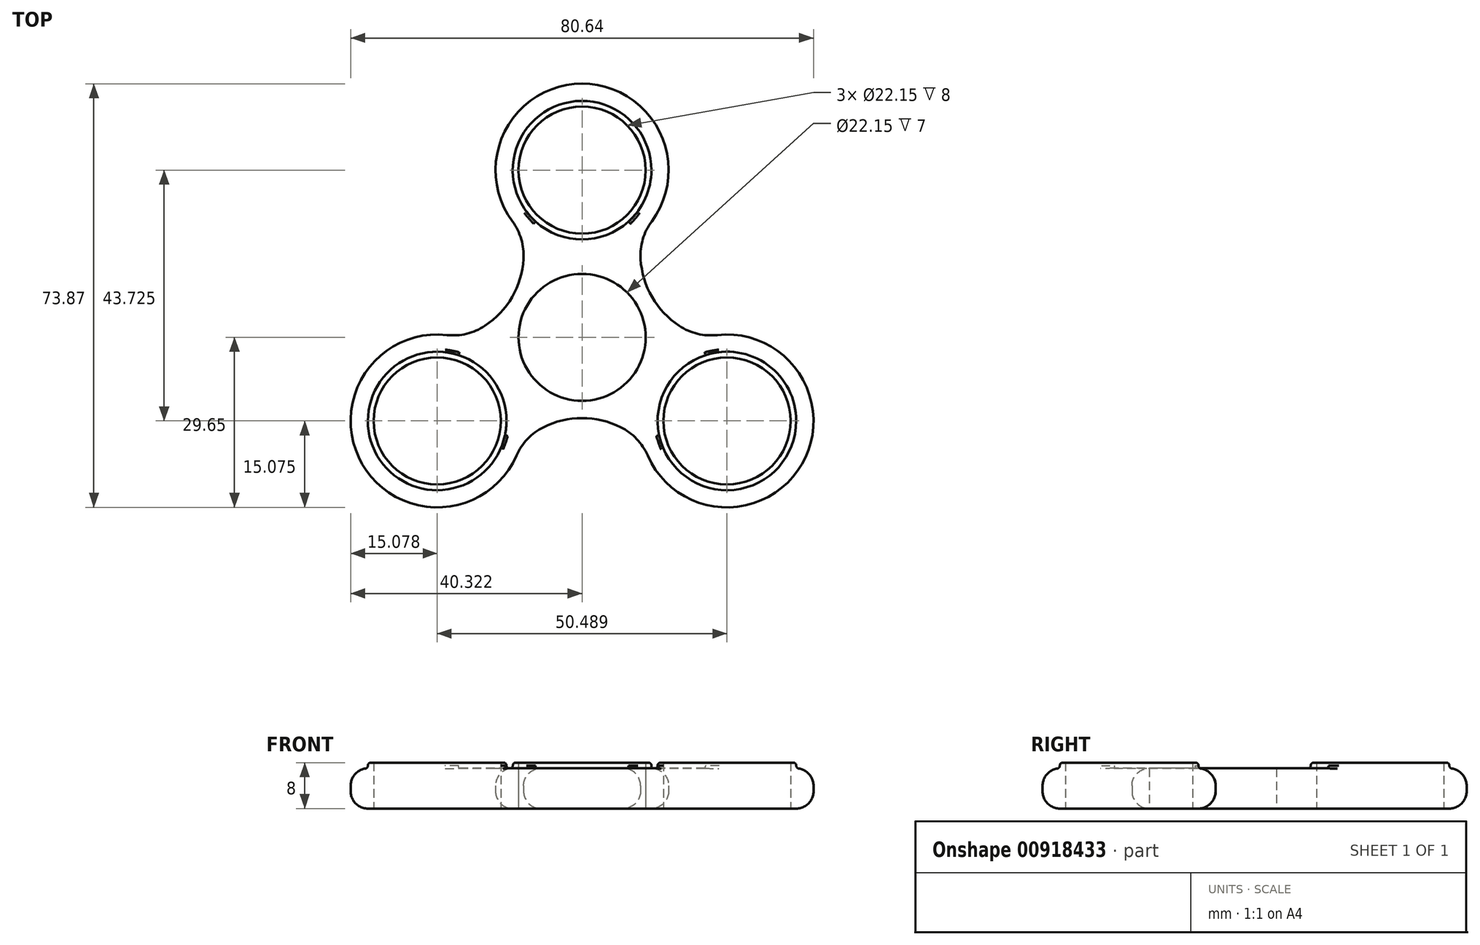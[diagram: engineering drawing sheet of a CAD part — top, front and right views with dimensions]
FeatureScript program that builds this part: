
annotation { "Feature Type Name" : "Feature", "Feature Type Description" : "" }
export const myFeature = defineFeature(function(context is Context, id is Id, definition is map)
    precondition{}
    {
        {
            var Q0;
            Q0=qCreatedBy(makeId("Top.planeOp"),FACE);
            var sketch = newSketch(context, id + "F0", { "sketchPlane" : qUnion([Q0])});
            skCircle(sketch, "E0", {"center": v(-80.48, 0) * mm, "radius": 11.07 * mm});
            skCircle(sketch, "E1", {"center": v(-80.48, 29.15) * mm, "radius": 11.07 * mm});
            skArc(sketch, "E2.0", {"start": v(-69.78, 18.53) * mm, "mid": v(-80.48, 44.23) * mm, "end": v(-91.17, 18.53) * mm});
            skArc(sketch, "E3.0", {"start": v(-69.78, -18.53) * mm, "mid": v(-80.48, -14.08) * mm, "end": v(-91.17, -18.53) * mm});
            skArc(sketch, "E4.0", {"start": v(-69.78, 18.53) * mm, "mid": v(-68.29, 7.04) * mm, "end": v(-59.08, 0) * mm});
            skCircle(sketch, "E5", {"center": v(-105.72, -14.58) * mm, "radius": 11.07 * mm});
            skArc(sketch, "E6.0", {"start": v(-101.87, 0) * mm, "mid": v(-118.78, -22.11) * mm, "end": v(-91.17, -18.53) * mm});
            skLineSegment(sketch, "E7.0", {"start": v(-105.72, -14.58) * mm, "end": v(-55.23, 14.58) * mm, "construction": true});
            skArc(sketch, "E8.0", {"start": v(-101.87, 0) * mm, "mid": v(-92.67, 7.04) * mm, "end": v(-91.17, 18.53) * mm});
            skCircle(sketch, "E9", {"center": v(-55.23, -14.58) * mm, "radius": 11.07 * mm});
            skArc(sketch, "E10.0", {"start": v(-69.78, -18.53) * mm, "mid": v(-42.18, -22.11) * mm, "end": v(-59.08, 0) * mm});
            skLineSegment(sketch, "E11.0", {"start": v(-55.23, -14.58) * mm, "end": v(-105.72, 14.58) * mm, "construction": true});
            skCircle(sketch, "E12.0", {"center": v(-80.48, 29.15) * mm, "radius": 12.07 * mm});
            skCircle(sketch, "E13.0", {"center": v(-55.23, -14.58) * mm, "radius": 12.07 * mm});
            skCircle(sketch, "E14.0", {"center": v(-105.72, -14.58) * mm, "radius": 12.07 * mm});
            skSolve(sketch);
        }
        {
            var Q0;
            Q0=makeQuery(id+"F0.imprint","IMPRINT",FACE,{"disambiguationData":[TD([[makeQuery(id+"F0.imprint","IMPRINT",EDGE,{"derivedFrom":sQuery(id+"F0.wireOp",EDGE,"E1")}),-1.0]])]});
            var Q1;
            Q1=makeQuery(id+"F0.imprint","IMPRINT",FACE,{"disambiguationData":[TD([[makeQuery(id+"F0.imprint","IMPRINT",EDGE,{"derivedFrom":sQuery(id+"F0.wireOp",EDGE,"E5")}),-1.0]])]});
            var Q2;
            Q2=makeQuery(id+"F0.imprint","IMPRINT",FACE,{"disambiguationData":[TD([[makeQuery(id+"F0.imprint","IMPRINT",EDGE,{"derivedFrom":sQuery(id+"F0.wireOp",EDGE,"E9")}),-1.0]])]});
            extrude(context, id + "F1", {"entities" : qUnion([Q0, Q1, Q2]), "depth" : 8 * mm, "offsetDistance" : 25 * mm});
        }
        {
            var Q0;
            Q0=makeQuery(id+"F0.imprint","IMPRINT",FACE,{"disambiguationData":[TD([[makeQuery(id+"F0.imprint","IMPRINT",EDGE,{"derivedFrom":sQuery(id+"F0.wireOp",EDGE,"E2.0")}),1.0]])]});
            extrude(context, id + "F2", {"entities" : qUnion([Q0]), "depth" : 7 * mm, "offsetDistance" : 25 * mm});
        }
        {
            var Q0;
            Q0=makeQuery(id+"F1.opExtrude","SWEPT_BODY",BODY,{"disambiguationData":[OSD([sQuery(id+"F0.wireOp",EDGE,"E1"),sQuery(id+"F0.wireOp",EDGE,"E12.0")])]});
            var Q1;
            Q1=makeQuery(id+"F1.opExtrude","SWEPT_BODY",BODY,{"disambiguationData":[OSD([sQuery(id+"F0.wireOp",EDGE,"E5"),sQuery(id+"F0.wireOp",EDGE,"E14.0")])]});
            var Q2;
            Q2=makeQuery(id+"F1.opExtrude","SWEPT_BODY",BODY,{"disambiguationData":[OSD([sQuery(id+"F0.wireOp",EDGE,"E9"),sQuery(id+"F0.wireOp",EDGE,"E13.0")])]});
            var Q3;
            Q3=makeQuery(id+"F2.opExtrude","SWEPT_BODY",BODY,{"disambiguationData":[OSD([sQuery(id+"F0.wireOp",EDGE,"E2.0"),sQuery(id+"F0.wireOp",EDGE,"E3.0"),sQuery(id+"F0.wireOp",EDGE,"E4.0"),sQuery(id+"F0.wireOp",EDGE,"E6.0"),sQuery(id+"F0.wireOp",EDGE,"E0"),sQuery(id+"F0.wireOp",EDGE,"E8.0"),sQuery(id+"F0.wireOp",EDGE,"E10.0"),sQuery(id+"F0.wireOp",EDGE,"E12.0"),sQuery(id+"F0.wireOp",EDGE,"E13.0"),sQuery(id+"F0.wireOp",EDGE,"E14.0")])]});
            booleanBodies(context, id + "F3", {"operationType" : BooleanOperationType.UNION, "tools" : qUnion([Q0, Q1, Q2, Q3])});
        }
        {
            var Q0;
            Q0=makeQuery(id+"F2.opExtrude","SWEPT_EDGE",EDGE,{"disambiguationData":[OSD([sQuery(id+"F0.wireOp",EDGE,"E3.0"),sQuery(id+"F0.wireOp",EDGE,"E6.0")])]});
            var Q1;
            Q1=makeQuery(id+"F2.opExtrude","SWEPT_EDGE",EDGE,{"disambiguationData":[OSD([sQuery(id+"F0.wireOp",EDGE,"E3.0"),sQuery(id+"F0.wireOp",EDGE,"E10.0")])]});
            var Q2;
            Q2=makeQuery(id+"F2.opExtrude","SWEPT_EDGE",EDGE,{"disambiguationData":[OSD([sQuery(id+"F0.wireOp",EDGE,"E2.0"),sQuery(id+"F0.wireOp",EDGE,"E4.0")])]});
            var Q3;
            Q3=makeQuery(id+"F2.opExtrude","SWEPT_EDGE",EDGE,{"disambiguationData":[OSD([sQuery(id+"F0.wireOp",EDGE,"E4.0"),sQuery(id+"F0.wireOp",EDGE,"E10.0")])]});
            var Q4;
            Q4=makeQuery(id+"F2.opExtrude","SWEPT_EDGE",EDGE,{"disambiguationData":[OSD([sQuery(id+"F0.wireOp",EDGE,"E2.0"),sQuery(id+"F0.wireOp",EDGE,"E8.0")])]});
            var Q5;
            Q5=makeQuery(id+"F2.opExtrude","SWEPT_EDGE",EDGE,{"disambiguationData":[OSD([sQuery(id+"F0.wireOp",EDGE,"E6.0"),sQuery(id+"F0.wireOp",EDGE,"E8.0")])]});
            fillet(context, id + "F4", {"entities" : qUnion([Q0, Q1, Q2, Q3, Q4, Q5]), "radius" : 10 * mm, "tangentPropagation" : true, "allowEdgeOverflow" : false});
        }
        {
            var Q0;
            {var subQ0=sQuery(id+"F0.wireOp",EDGE,"E4.0");var subQ1=sQuery(id+"F0.wireOp",EDGE,"E2.0");Q0=makeQuery(id+"F4.opFillet","BLEND_EDGE",EDGE,{"blendedFrom":[makeQuery(id+"F2.opExtrude","SWEPT_EDGE",EDGE,{"disambiguationData":[OSD([subQ1,subQ0])]}),makeQuery(id+"F2.opExtrude","CAP_FACE",FACE,{"disambiguationData":[OSD([subQ1,sQuery(id+"F0.wireOp",EDGE,"E3.0"),subQ0,sQuery(id+"F0.wireOp",EDGE,"E6.0"),sQuery(id+"F0.wireOp",EDGE,"E0"),sQuery(id+"F0.wireOp",EDGE,"E8.0"),sQuery(id+"F0.wireOp",EDGE,"E10.0"),sQuery(id+"F0.wireOp",EDGE,"E12.0"),sQuery(id+"F0.wireOp",EDGE,"E13.0"),sQuery(id+"F0.wireOp",EDGE,"E14.0")])],"isStart":false})],"blendedInto":[makeQuery(id+"F2.opExtrude","CAP_FACE",FACE,{"disambiguationData":[OSD([subQ1,sQuery(id+"F0.wireOp",EDGE,"E3.0"),subQ0,sQuery(id+"F0.wireOp",EDGE,"E6.0"),sQuery(id+"F0.wireOp",EDGE,"E0"),sQuery(id+"F0.wireOp",EDGE,"E8.0"),sQuery(id+"F0.wireOp",EDGE,"E10.0"),sQuery(id+"F0.wireOp",EDGE,"E12.0"),sQuery(id+"F0.wireOp",EDGE,"E13.0"),sQuery(id+"F0.wireOp",EDGE,"E14.0")])],"isStart":false})]});}
            var Q1;
            {var subQ0=sQuery(id+"F0.wireOp",EDGE,"E14.0");var subQ1=sQuery(id+"F0.wireOp",EDGE,"E13.0");var subQ2=sQuery(id+"F0.wireOp",EDGE,"E12.0");var subQ3=sQuery(id+"F0.wireOp",EDGE,"E4.0");var subQ4=sQuery(id+"F0.wireOp",EDGE,"E2.0");Q1=makeQuery(id+"F4.opFillet","BLEND_EDGE",EDGE,{"blendedFrom":[makeQuery(id+"F2.opExtrude","SWEPT_EDGE",EDGE,{"disambiguationData":[OSD([subQ4,subQ3])]}),makeQuery(id+"F3.opBoolean","MERGE",FACE,{"derivedFrom":[makeQuery(id+"F1.opExtrude","CAP_FACE",FACE,{"disambiguationData":[OSD([sQuery(id+"F0.wireOp",EDGE,"E1"),subQ2])],"isStart":true}),makeQuery(id+"F1.opExtrude","CAP_FACE",FACE,{"disambiguationData":[OSD([sQuery(id+"F0.wireOp",EDGE,"E5"),subQ0])],"isStart":true}),makeQuery(id+"F1.opExtrude","CAP_FACE",FACE,{"disambiguationData":[OSD([sQuery(id+"F0.wireOp",EDGE,"E9"),subQ1])],"isStart":true}),makeQuery(id+"F2.opExtrude","CAP_FACE",FACE,{"disambiguationData":[OSD([subQ4,sQuery(id+"F0.wireOp",EDGE,"E3.0"),subQ3,sQuery(id+"F0.wireOp",EDGE,"E6.0"),sQuery(id+"F0.wireOp",EDGE,"E0"),sQuery(id+"F0.wireOp",EDGE,"E8.0"),sQuery(id+"F0.wireOp",EDGE,"E10.0"),subQ2,subQ1,subQ0])],"isStart":true})]})],"blendedInto":[makeQuery(id+"F3.opBoolean","MERGE",FACE,{"derivedFrom":[makeQuery(id+"F1.opExtrude","CAP_FACE",FACE,{"disambiguationData":[OSD([sQuery(id+"F0.wireOp",EDGE,"E1"),subQ2])],"isStart":true}),makeQuery(id+"F1.opExtrude","CAP_FACE",FACE,{"disambiguationData":[OSD([sQuery(id+"F0.wireOp",EDGE,"E5"),subQ0])],"isStart":true}),makeQuery(id+"F1.opExtrude","CAP_FACE",FACE,{"disambiguationData":[OSD([sQuery(id+"F0.wireOp",EDGE,"E9"),subQ1])],"isStart":true}),makeQuery(id+"F2.opExtrude","CAP_FACE",FACE,{"disambiguationData":[OSD([subQ4,sQuery(id+"F0.wireOp",EDGE,"E3.0"),subQ3,sQuery(id+"F0.wireOp",EDGE,"E6.0"),sQuery(id+"F0.wireOp",EDGE,"E0"),sQuery(id+"F0.wireOp",EDGE,"E8.0"),sQuery(id+"F0.wireOp",EDGE,"E10.0"),subQ2,subQ1,subQ0])],"isStart":true})]})]});}
            fillet(context, id + "F5", {"entities" : qUnion([Q0, Q1]), "radius" : 3 * mm, "tangentPropagation" : true, "allowEdgeOverflow" : false});
        }
        {
            var Q0;
            Q0=makeQuery(id+"F1.opExtrude","CAP_EDGE",EDGE,{"disambiguationData":[OSD([sQuery(id+"F0.wireOp",EDGE,"E14.0")])],"isStart":false});
            var Q1;
            Q1=makeQuery(id+"F1.opExtrude","CAP_EDGE",EDGE,{"disambiguationData":[OSD([sQuery(id+"F0.wireOp",EDGE,"E12.0")])],"isStart":false});
            var Q2;
            Q2=makeQuery(id+"F1.opExtrude","CAP_EDGE",EDGE,{"disambiguationData":[OSD([sQuery(id+"F0.wireOp",EDGE,"E13.0")])],"isStart":false});
            var Q3;
            Q3=makeQuery(id+"F5.opFillet","BLEND_EDGE",EDGE,{"blendedFrom":[makeQuery(id+"F2.opExtrude","CAP_EDGE",EDGE,{"disambiguationData":[OSD([sQuery(id+"F0.wireOp",EDGE,"E10.0")])],"isStart":false}),makeQuery(id+"F1.opExtrude","SWEPT_FACE",FACE,{"disambiguationData":[OSD([sQuery(id+"F0.wireOp",EDGE,"E13.0")])]})],"blendedInto":[makeQuery(id+"F1.opExtrude","SWEPT_FACE",FACE,{"disambiguationData":[OSD([sQuery(id+"F0.wireOp",EDGE,"E13.0")])]})]});
            var Q4;
            Q4=makeQuery(id+"F5.opFillet","BLEND_EDGE",EDGE,{"blendedFrom":[makeQuery(id+"F2.opExtrude","CAP_EDGE",EDGE,{"disambiguationData":[OSD([sQuery(id+"F0.wireOp",EDGE,"E2.0")])],"isStart":false}),makeQuery(id+"F1.opExtrude","SWEPT_FACE",FACE,{"disambiguationData":[OSD([sQuery(id+"F0.wireOp",EDGE,"E12.0")])]})],"blendedInto":[makeQuery(id+"F1.opExtrude","SWEPT_FACE",FACE,{"disambiguationData":[OSD([sQuery(id+"F0.wireOp",EDGE,"E12.0")])]})]});
            var Q5;
            Q5=makeQuery(id+"F2.opExtrude","CAP_EDGE",EDGE,{"disambiguationData":[OSD([sQuery(id+"F0.wireOp",EDGE,"E13.0")])],"isStart":false});
            var Q6;
            Q6=makeQuery(id+"F1.opExtrude","SWEPT_FACE",FACE,{"disambiguationData":[OSD([sQuery(id+"F0.wireOp",EDGE,"E12.0")])]});
            var Q7;
            Q7=makeQuery(id+"F2.opExtrude","CAP_EDGE",EDGE,{"disambiguationData":[OSD([sQuery(id+"F0.wireOp",EDGE,"E14.0")])],"isStart":false});
            var Q8;
            Q8=makeQuery(id+"F5.opFillet","BLEND_EDGE",EDGE,{"blendedFrom":[makeQuery(id+"F2.opExtrude","CAP_EDGE",EDGE,{"disambiguationData":[OSD([sQuery(id+"F0.wireOp",EDGE,"E6.0")])],"isStart":false}),makeQuery(id+"F1.opExtrude","SWEPT_FACE",FACE,{"disambiguationData":[OSD([sQuery(id+"F0.wireOp",EDGE,"E14.0")])]})],"blendedInto":[makeQuery(id+"F1.opExtrude","SWEPT_FACE",FACE,{"disambiguationData":[OSD([sQuery(id+"F0.wireOp",EDGE,"E14.0")])]})]});
            fillet(context, id + "F6", {"entities" : qUnion([Q0, Q1, Q2, Q3, Q4, Q5, Q6, Q7, Q8]), "radius" : .5 * mm, "tangentPropagation" : true, "allowEdgeOverflow" : false});
        }
    });
